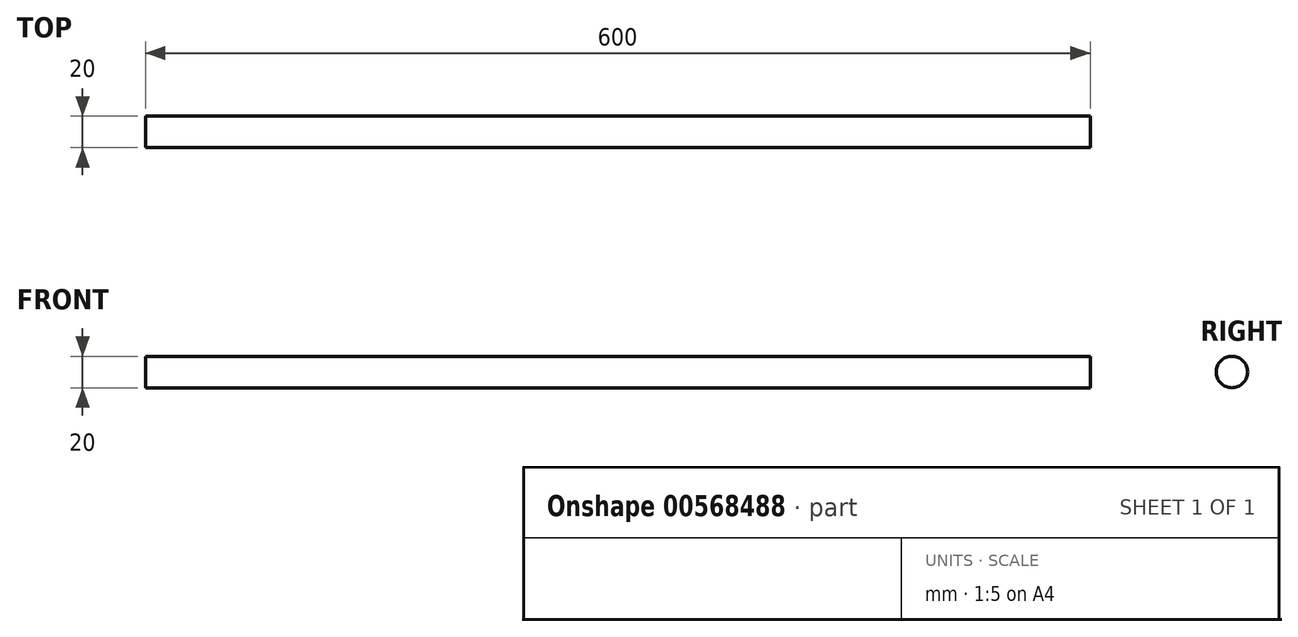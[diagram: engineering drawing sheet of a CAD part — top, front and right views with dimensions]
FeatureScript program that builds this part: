
annotation { "Feature Type Name" : "Feature", "Feature Type Description" : "" }
export const myFeature = defineFeature(function(context is Context, id is Id, definition is map)
    precondition{}
    {
        {
            var Q0;
            Q0=qCreatedBy(makeId("Front.planeOp"),FACE);
            var sketch = newSketch(context, id + "F0", { "sketchPlane" : qUnion([Q0])});
            skLineSegment(sketch, "E0", {"start": v(0, 0) * mm, "end": v(-300, 0) * mm, "construction": true});
            skLineSegment(sketch, "E1", {"start": v(-300, 0) * mm, "end": v(-300, 10) * mm});
            skLineSegment(sketch, "E2", {"start": v(-300, 10) * mm, "end": v(0, 10) * mm});
            skLineSegment(sketch, "E3", {"start": v(0, 10) * mm, "end": v(0, 0) * mm});
            skLineSegment(sketch, "E4", {"start": v(-300, 0) * mm, "end": v(0, 0) * mm});
            skSolve(sketch);
        }
        {
            var Q0;
            Q0=makeQuery(id+"F0.imprint","IMPRINT",FACE,{"disambiguationData":[TD([[makeQuery(id+"F0.imprint","IMPRINT",EDGE,{"derivedFrom":sQuery(id+"F0.wireOp",EDGE,"E1")}),-1.0]])]});
            var Q1;
            Q1=sQuery(id+"F0.wireOp",EDGE,"E4");
            revolve(context, id + "F1", {"entities" : qUnion([Q0]), "axis" : qUnion([Q1]), "revolveType" : RevolveType.FULL});
        }
        {
            var Q0;
            Q0=makeQuery(id+"F1.opRevolve","SWEPT_BODY",BODY,{"disambiguationData":[OSD([sQuery(id+"F0.wireOp",EDGE,"E1"),sQuery(id+"F0.wireOp",EDGE,"E2"),sQuery(id+"F0.wireOp",EDGE,"E3"),sQuery(id+"F0.wireOp",EDGE,"E4")])]});
            var Q1;
            Q1=qCreatedBy(makeId("Right.planeOp"),FACE);
            mirror(context, id + "F2", {"operationType" : NewBodyOperationType.ADD, "entities" : qUnion([Q0]), "mirrorPlane" : qUnion([Q1])});
        }
    });
